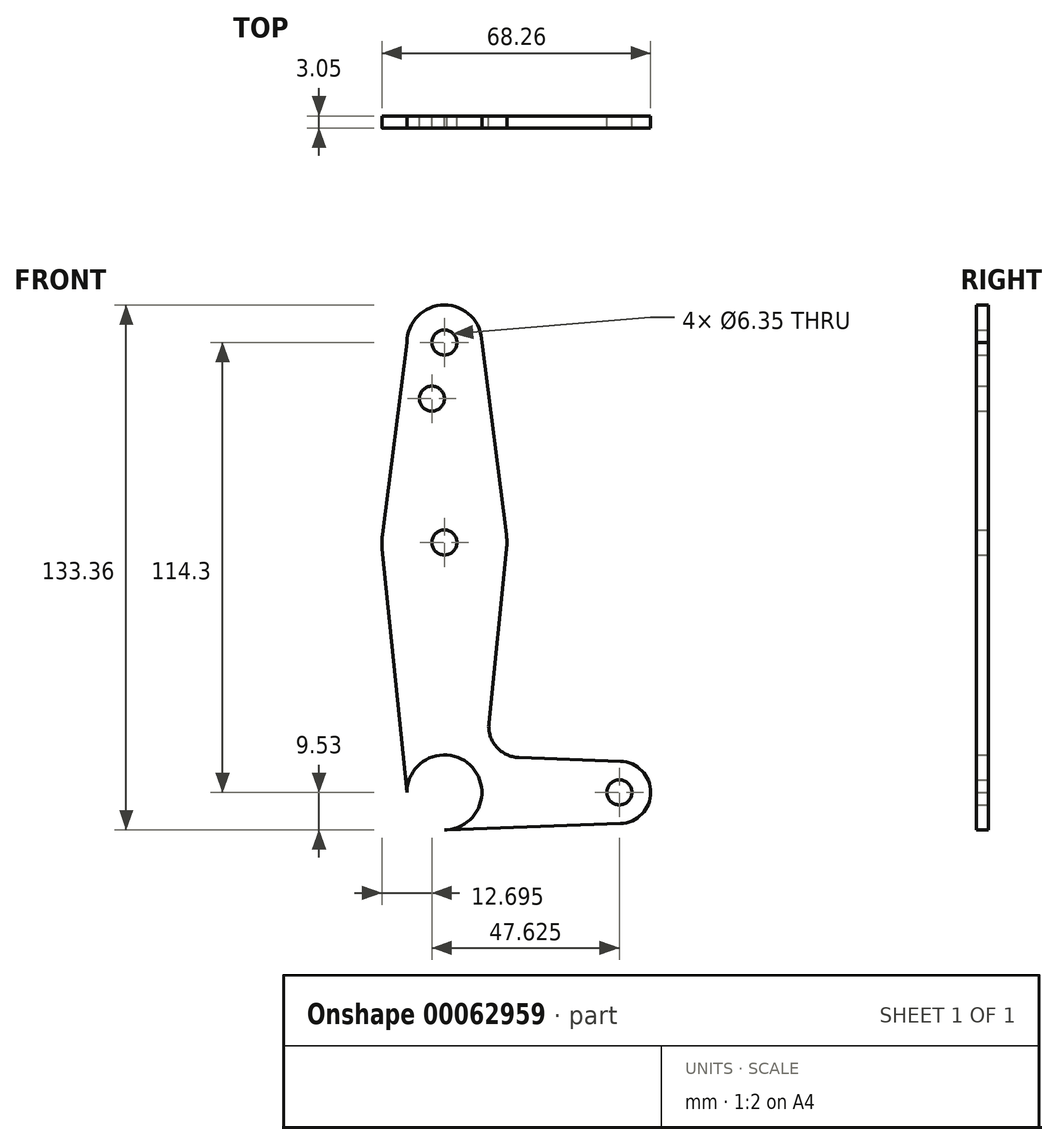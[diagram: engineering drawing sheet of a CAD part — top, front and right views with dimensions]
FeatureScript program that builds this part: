
annotation { "Feature Type Name" : "Feature", "Feature Type Description" : "" }
export const myFeature = defineFeature(function(context is Context, id is Id, definition is map)
    precondition{}
    {
        {
            var Q0;
            Q0=qCreatedBy(makeId("Front.planeOp"),FACE);
            var sketch = newSketch(context, id + "F0", { "sketchPlane" : qUnion([Q0])});
            skCircle(sketch, "E0", {"center": v(0, 0) * mm, "radius": 9.53 * mm});
            skCircle(sketch, "E1", {"center": v(0, 114.3) * mm, "radius": 9.53 * mm});
            skCircle(sketch, "E2", {"center": v(0, 63.5) * mm, "radius": 15.88 * mm});
            skCircle(sketch, "E3", {"center": v(44.45, 0) * mm, "radius": 7.94 * mm});
            skLineSegment(sketch, "E4", {"start": v(0, 114.3) * mm, "end": v(0, 0) * mm, "construction": true});
            skLineSegment(sketch, "E5", {"start": v(0, 0) * mm, "end": v(44.45, 0) * mm, "construction": true});
            skLineSegment(sketch, "E6", {"start": v(0, -9.53) * mm, "end": v(44.73, -7.93) * mm});
            skCircle(sketch, "E7", {"center": v(0, 114.3) * mm, "radius": 3.18 * mm});
            skCircle(sketch, "E8", {"center": v(0, 63.5) * mm, "radius": 3.18 * mm});
            skCircle(sketch, "E9", {"center": v(44.45, 0) * mm, "radius": 3.18 * mm});
            skCircle(sketch, "E10", {"center": v(-3.17, 100.03) * mm, "radius": 3.18 * mm});
            skPoint(sketch, "E11.newPointA", {"position": v(9.53, 0) * mm});
            skPoint(sketch, "E11.newPointB", {"position": v(0, 9.52) * mm});
            skLineSegment(sketch, "E12", {"start": v(11.3, 17.6) * mm, "end": v(15.8, 61.9) * mm});
            skLineSegment(sketch, "E13", {"start": v(18.93, 8.85) * mm, "end": v(44.73, 7.93) * mm});
            skArc(sketch, "E14.filletArc", {"start": v(11.3, 17.6) * mm, "mid": v(13.22, 11.57) * mm, "end": v(18.93, 8.85) * mm});
            skLineSegment(sketch, "E15", {"start": v(-9.53, 114.3) * mm, "end": v(9.52, 114.3) * mm, "construction": true});
            skLineSegment(sketch, "E16", {"start": v(9.52, 114.3) * mm, "end": v(15.75, 65.5) * mm});
            skLineSegment(sketch, "E17", {"start": v(-9.52, 114.3) * mm, "end": v(-15.75, 65.5) * mm});
            skLineSegment(sketch, "E18", {"start": v(-9.53, 0) * mm, "end": v(-15.8, 61.9) * mm});
            skCircle(sketch, "E19", {"center": v(0, 0) * mm, "radius": 3.18 * mm});
            skSolve(sketch);
        }
        {
            var Q0;
            Q0=makeQuery(id+"F0.imprint","IMPRINT",FACE,{"disambiguationData":[TD([[makeQuery(id+"F0.imprint","IMPRINT",EDGE,{"derivedFrom":sQuery(id+"F0.wireOp",EDGE,"E8")}),-1.0]])]});
            var Q1;
            Q1=makeQuery(id+"F0.imprint","IMPRINT",FACE,{"disambiguationData":[TD([[makeQuery(id+"F0.imprint","IMPRINT",EDGE,{"derivedFrom":sQuery(id+"F0.wireOp",EDGE,"E10")}),-1.0]])]});
            var Q2;
            {var subQ7=sQuery(id+"F0.wireOp",EDGE,"E12");Q2=makeQuery(id+"F0.imprint","IMPRINT",FACE,{"disambiguationData":[TD([[makeQuery(id+"F0.imprint","IMPRINT",EDGE,{"derivedFrom":subQ7}),1.0]])]});}
            var Q3;
            Q3=makeQuery(id+"F0.imprint","IMPRINT",FACE,{"disambiguationData":[TD([[makeQuery(id+"F0.imprint","IMPRINT",EDGE,{"derivedFrom":sQuery(id+"F0.wireOp",EDGE,"E7")}),-1.0]])]});
            var Q4;
            Q4=makeQuery(id+"F0.imprint","IMPRINT",FACE,{"disambiguationData":[TD([[makeQuery(id+"F0.imprint","IMPRINT",EDGE,{"derivedFrom":sQuery(id+"F0.wireOp",EDGE,"E9")}),-1.0]])]});
            var Q5;
            {var subQ0=sQuery(id+"F0.wireOp",EDGE,"E6");var subQ1=sQuery(id+"F0.wireOp",EDGE,"E0");var subQ2=makeQuery(id+"F0.imprint","INTERSECT",VERTEX,{"disambiguationData":[OD(0.0)],"derivedFrom":[subQ1,subQ0]});Q5=makeQuery(id+"F0.imprint","IMPRINT",FACE,{"disambiguationData":[TD([[makeQuery(id+"F0.imprint","IMPRINT",EDGE,{"disambiguationData":[TD([[subQ2,1.0]])],"derivedFrom":subQ1}),1.0]])]});}
            extrude(context, id + "F1", {"entities" : qUnion([Q0, Q1, Q2, Q3, Q4, Q5]), "depth" : 3.05 * mm});
        }
    });
